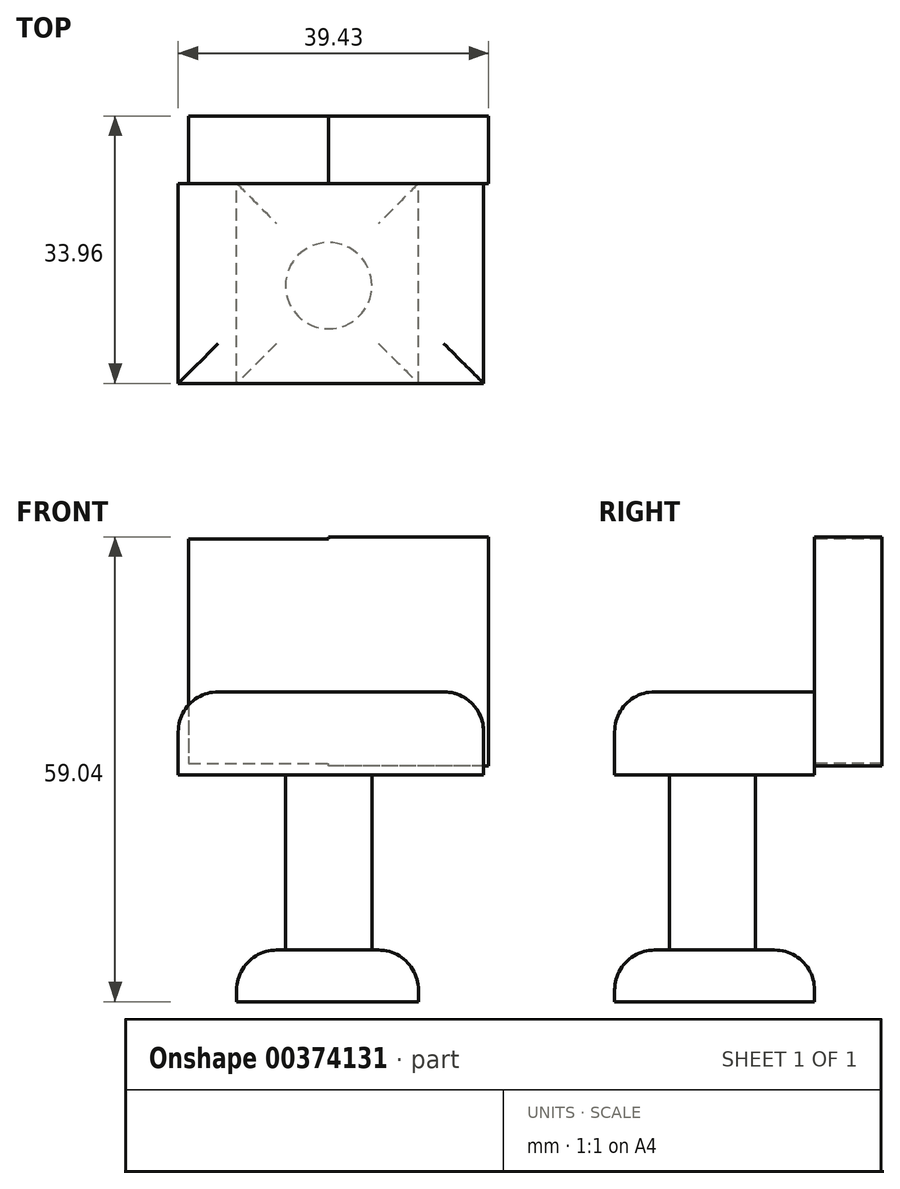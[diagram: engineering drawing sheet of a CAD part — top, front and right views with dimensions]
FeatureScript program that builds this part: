
annotation { "Feature Type Name" : "Feature", "Feature Type Description" : "" }
export const myFeature = defineFeature(function(context is Context, id is Id, definition is map)
    precondition{}
    {
        {
            var Q0;
            Q0=qCreatedBy(makeId("Front.planeOp"),FACE);
            var sketch = newSketch(context, id + "F0", { "sketchPlane" : qUnion([Q0])});
            skLineSegment(sketch, "E0.bottom", {"start": v(-19.11, 5) * mm, "end": v(19.68, 5) * mm});
            skLineSegment(sketch, "E0.top", {"start": v(-19.11, -5.56) * mm, "end": v(19.68, -5.56) * mm});
            skLineSegment(sketch, "E0.left", {"start": v(-19.11, 5) * mm, "end": v(-19.11, -5.56) * mm});
            skLineSegment(sketch, "E0.right", {"start": v(19.68, 5) * mm, "end": v(19.68, -5.56) * mm});
            skSolve(sketch);
        }
        {
            var Q0;
            Q0 = qSketchRegion(id + "F0", true);
            extrude(context, id + "F1", {"entities" : qUnion([Q0]), "depth" : 25.4 * mm});
        }
        {
            var Q0;
            Q0=qCreatedBy(makeId("Right.planeOp"),FACE);
            var sketch = newSketch(context, id + "F2", { "sketchPlane" : qUnion([Q0])});
            skLineSegment(sketch, "E1.bottom", {"start": v(0, -4.42) * mm, "end": v(8.56, -4.42) * mm});
            skLineSegment(sketch, "E1.top", {"start": v(0, 24.67) * mm, "end": v(8.56, 24.67) * mm});
            skLineSegment(sketch, "E1.left", {"start": v(0, -4.42) * mm, "end": v(0, 24.67) * mm});
            skLineSegment(sketch, "E1.right", {"start": v(8.56, -4.42) * mm, "end": v(8.56, 24.67) * mm});
            skSolve(sketch);
        }
        {
            var Q0;
            Q0 = qSketchRegion(id + "F2", true);
            extrude(context, id + "F3", {"entities" : qUnion([Q0]), "operationType" : NewBodyOperationType.ADD, "depth" : 20.32 * mm});
        }
        {
            var Q0;
            Q0=qCreatedBy(makeId("Right.planeOp"),FACE);
            var sketch = newSketch(context, id + "F4", { "sketchPlane" : qUnion([Q0])});
            skLineSegment(sketch, "E2.bottom", {"start": v(8.56, 24.39) * mm, "end": v(0, 24.39) * mm});
            skLineSegment(sketch, "E2.top", {"start": v(8.56, -4.14) * mm, "end": v(0, -4.14) * mm});
            skLineSegment(sketch, "E2.left", {"start": v(8.56, 24.39) * mm, "end": v(8.56, -4.14) * mm});
            skLineSegment(sketch, "E2.right", {"start": v(0, 24.39) * mm, "end": v(0, -4.14) * mm});
            skSolve(sketch);
        }
        {
            var Q0;
            Q0 = qSketchRegion(id + "F4", true);
            extrude(context, id + "F5", {"entities" : qUnion([Q0]), "operationType" : NewBodyOperationType.ADD, "oppositeDirection" : true, "depth" : 17.78 * mm});
        }
        {
            var Q0;
            Q0=qCreatedBy(makeId("Top.planeOp"),FACE);
            var sketch = newSketch(context, id + "F6", { "sketchPlane" : qUnion([Q0])});
            skCircle(sketch, "E3", {"center": v(0, -12.98) * mm, "radius": 5.48 * mm});
            skSolve(sketch);
        }
        {
            var Q0;
            Q0 = qSketchRegion(id + "F6", true);
            extrude(context, id + "F7", {"entities" : qUnion([Q0]), "operationType" : NewBodyOperationType.ADD, "oppositeDirection" : true, "depth" : 27.94 * mm});
        }
        {
            var Q0;
            Q0=qCreatedBy(makeId("Front.planeOp"),FACE);
            var sketch = newSketch(context, id + "F8", { "sketchPlane" : qUnion([Q0])});
            skLineSegment(sketch, "E4.bottom", {"start": v(-11.7, -34.37) * mm, "end": v(11.4, -34.37) * mm});
            skLineSegment(sketch, "E4.top", {"start": v(-11.7, -27.81) * mm, "end": v(11.4, -27.81) * mm});
            skLineSegment(sketch, "E4.left", {"start": v(-11.7, -34.37) * mm, "end": v(-11.7, -27.81) * mm});
            skLineSegment(sketch, "E4.right", {"start": v(11.4, -34.37) * mm, "end": v(11.4, -27.81) * mm});
            skSolve(sketch);
        }
        {
            var Q0;
            Q0 = qSketchRegion(id + "F8", true);
            extrude(context, id + "F9", {"entities" : qUnion([Q0]), "operationType" : NewBodyOperationType.ADD, "depth" : 25.4 * mm});
        }
        {
            var Q0;
            Q0=makeQuery(id+"F1.opExtrude","CAP_EDGE",EDGE,{"disambiguationData":[OSD([sQuery(id+"F0.wireOp",EDGE,"E0.bottom")])],"isStart":false});
            var Q1;
            Q1=makeQuery(id+"F1.opExtrude","SWEPT_EDGE",EDGE,{"disambiguationData":[OSD([sQuery(id+"F0.wireOp",EDGE,"E0.bottom"),sQuery(id+"F0.wireOp",EDGE,"E0.left")])]});
            var Q2;
            Q2=makeQuery(id+"F1.opExtrude","SWEPT_EDGE",EDGE,{"disambiguationData":[OSD([sQuery(id+"F0.wireOp",EDGE,"E0.bottom"),sQuery(id+"F0.wireOp",EDGE,"E0.right")])]});
            var Q3;
            Q3=makeQuery(id+"F9.opExtrude","CAP_EDGE",EDGE,{"disambiguationData":[OSD([sQuery(id+"F8.wireOp",EDGE,"E4.top")])],"isStart":false});
            var Q4;
            Q4=makeQuery(id+"F9.opExtrude","SWEPT_EDGE",EDGE,{"disambiguationData":[OSD([sQuery(id+"F8.wireOp",EDGE,"E4.top"),sQuery(id+"F8.wireOp",EDGE,"E4.right")])]});
            var Q5;
            Q5=makeQuery(id+"F9.opExtrude","SWEPT_EDGE",EDGE,{"disambiguationData":[OSD([sQuery(id+"F8.wireOp",EDGE,"E4.top"),sQuery(id+"F8.wireOp",EDGE,"E4.left")])]});
            var Q6;
            Q6=makeQuery(id+"F9.opExtrude","CAP_EDGE",EDGE,{"disambiguationData":[OSD([sQuery(id+"F8.wireOp",EDGE,"E4.top")])],"isStart":true});
            fillet(context, id + "F10", {"entities" : qUnion([Q0, Q1, Q2, Q3, Q4, Q5, Q6]), "radius" : 5.08 * mm, "tangentPropagation" : true, "allowEdgeOverflow" : false});
        }
    });
